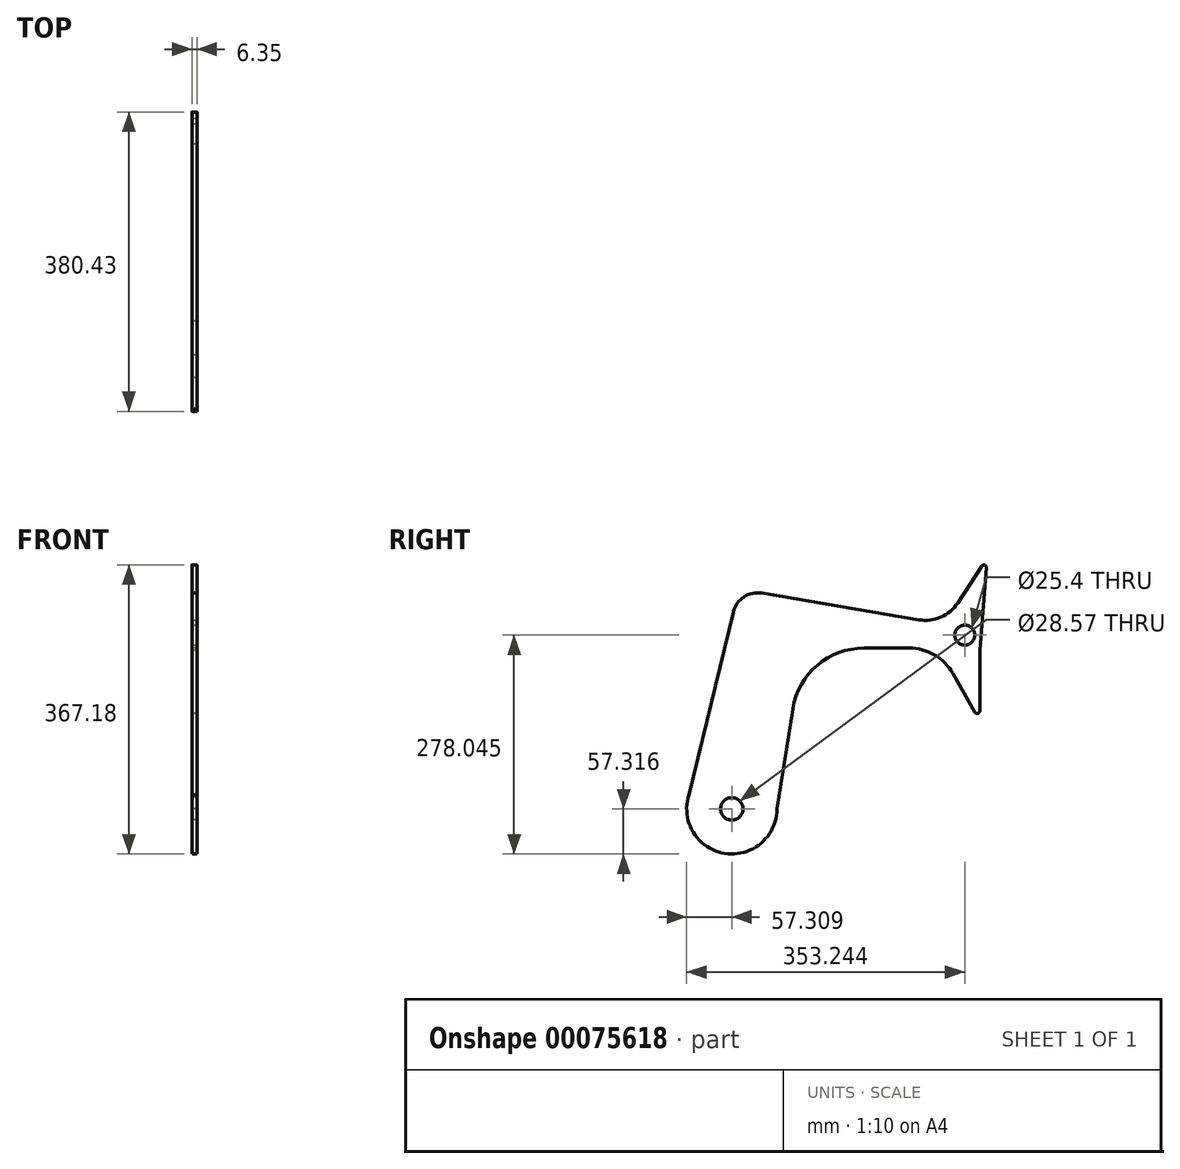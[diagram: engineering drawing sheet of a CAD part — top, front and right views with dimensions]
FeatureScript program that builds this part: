
annotation { "Feature Type Name" : "Feature", "Feature Type Description" : "" }
export const myFeature = defineFeature(function(context is Context, id is Id, definition is map)
    precondition{}
    {
        {
            var Q0;
            Q0=qCreatedBy(makeId("Right.planeOp"),FACE);
            var sketch = newSketch(context, id + "F0", { "sketchPlane" : qUnion([Q0])});
            skLineSegment(sketch, "E0", {"start": v(-2.1, -204.51) * mm, "end": v(18.16, -77.15) * mm});
            skLineSegment(sketch, "E1", {"start": v(108.55, 0) * mm, "end": v(165.98, 0) * mm});
            skLineSegment(sketch, "E2", {"start": v(255.1, -7.42) * mm, "end": v(263.7, 102.5) * mm});
            skLineSegment(sketch, "E3", {"start": v(258.45, 104.29) * mm, "end": v(227.65, 57.43) * mm});
            skLineSegment(sketch, "E4", {"start": v(178.24, 35.93) * mm, "end": v(-21.04, 69.81) * mm});
            skLineSegment(sketch, "E5", {"start": v(-57.64, 45.7) * mm, "end": v(-113.9, -186.5) * mm});
            skPoint(sketch, "E6.visualSharp", {"position": v(255.68, 0) * mm});
            skPoint(sketch, "E7.visualSharp", {"position": v(30.43, 0) * mm});
            skArc(sketch, "E7.filletArc", {"start": v(108.55, 0) * mm, "mid": v(49.13, -21.9) * mm, "end": v(18.16, -77.15) * mm});
            skPoint(sketch, "E8.visualSharp", {"position": v(-50.58, 74.84) * mm});
            skArc(sketch, "E8.filletArc", {"start": v(-21.04, 69.81) * mm, "mid": v(-44.09, 64.97) * mm, "end": v(-57.64, 45.7) * mm});
            skPoint(sketch, "E9.visualSharp", {"position": v(209.97, 30.54) * mm});
            skArc(sketch, "E9.filletArc", {"start": v(178.24, 35.93) * mm, "mid": v(206.15, 39.33) * mm, "end": v(227.65, 57.43) * mm});
            skLineSegment(sketch, "E10", {"start": v(255.46, 0) * mm, "end": v(255.46, -80.02) * mm});
            skLineSegment(sketch, "E11", {"start": v(249.32, -81.64) * mm, "end": v(221.44, -32.34) * mm});
            skPoint(sketch, "E12", {"position": v(182, 0) * mm});
            skPoint(sketch, "E13.visualSharp", {"position": v(-24.24, -343.7) * mm});
            skPoint(sketch, "E14.visualSharp", {"position": v(-149.22, -332.31) * mm});
            skPoint(sketch, "E15.newPointA", {"position": v(203.14, 0) * mm});
            skPoint(sketch, "E15.newPointB", {"position": v(255.46, 0) * mm});
            skArc(sketch, "E15.filletArc", {"start": v(221.44, -32.34) * mm, "mid": v(198.08, -8.68) * mm, "end": v(165.98, 0) * mm});
            skPoint(sketch, "E16.visualSharp", {"position": v(264.57, 113.6) * mm});
            skArc(sketch, "E16.filletArc", {"start": v(263.7, 102.5) * mm, "mid": v(261.77, 105.42) * mm, "end": v(258.45, 104.29) * mm});
            skPoint(sketch, "E17.visualSharp", {"position": v(255.46, -92.48) * mm});
            skArc(sketch, "E17.filletArc", {"start": v(255.41, -92.4) * mm, "mid": v(255.44, -92.4) * mm, "end": v(255.46, -92.39) * mm});
            skArc(sketch, "E18.filletArc", {"start": v(249.32, -81.64) * mm, "mid": v(253.01, -83.2) * mm, "end": v(255.46, -80.02) * mm});
            skCircle(sketch, "E19", {"center": v(-59.41, -204.28) * mm, "radius": 57.31 * mm});
            skCircle(sketch, "E20", {"center": v(-59.41, -204.28) * mm, "radius": 14.29 * mm});
            skSolve(sketch);
        }
        {
            var Q0;
            Q0=makeQuery(id+"F0.imprint","IMPRINT",FACE,{"disambiguationData":[TD([[makeQuery(id+"F0.imprint","IMPRINT",EDGE,{"derivedFrom":sQuery(id+"F0.wireOp",EDGE,"E0")}),1.0]])]});
            extrude(context, id + "F1", {"entities" : qUnion([Q0]), "depth" : 6.35 * mm});
        }
        {
            var Q0;
            {var subQ0=sQuery(id+"F0.wireOp",EDGE,"E10");Q0=makeQuery(id+"F0.imprint","IMPRINT",FACE,{"disambiguationData":[TD([[makeQuery(id+"F0.imprint","IMPRINT",EDGE,{"derivedFrom":subQ0}),-1.0]])]});}
            extrude(context, id + "F2", {"entities" : qUnion([Q0]), "operationType" : NewBodyOperationType.ADD, "depth" : 6.35 * mm});
        }
        {
            var Q0;
            Q0=makeQuery(id+"F1.opExtrude","CAP_FACE",FACE,{"disambiguationData":[OSD([sQuery(id+"F0.wireOp",EDGE,"E0"),sQuery(id+"F0.wireOp",EDGE,"E1"),sQuery(id+"F0.wireOp",EDGE,"E2"),sQuery(id+"F0.wireOp",EDGE,"E3"),sQuery(id+"F0.wireOp",EDGE,"E4"),sQuery(id+"F0.wireOp",EDGE,"E5"),sQuery(id+"F0.wireOp",EDGE,"E7.filletArc"),sQuery(id+"F0.wireOp",EDGE,"E8.filletArc"),sQuery(id+"F0.wireOp",EDGE,"E9.filletArc"),sQuery(id+"F0.wireOp",EDGE,"e1bb0cd2-49ca-4208-82d9-40ad98cda44d"),sQuery(id+"F0.wireOp",EDGE,"E10"),sQuery(id+"F0.wireOp",EDGE,"E11"),sQuery(id+"F0.wireOp",EDGE,"UkPQ0f5z-xmOE-aKsi-LPIj-pIVzT7c7XED3"),sQuery(id+"F0.wireOp",EDGE,"E13.filletArc"),sQuery(id+"F0.wireOp",EDGE,"E14.filletArc"),sQuery(id+"F0.wireOp",EDGE,"E15.filletArc")])],"isStart":false});
            var sketch = newSketch(context, id + "F3", { "sketchPlane" : qUnion([Q0])});
            skCircle(sketch, "E21", {"center": v(236.52, 16.45) * mm, "radius": 6.35 * mm});
            skSolve(sketch);
        }
        {
            var Q0;
            Q0=sQuery(id+"F3.wireOp",VERTEX,"E21.center");
            var Q1;
            Q1=makeQuery(id+"F1.opExtrude","SWEPT_BODY",BODY,{"disambiguationData":[OSD([sQuery(id+"F0.wireOp",EDGE,"E0"),sQuery(id+"F0.wireOp",EDGE,"E1"),sQuery(id+"F0.wireOp",EDGE,"E2"),sQuery(id+"F0.wireOp",EDGE,"E3"),sQuery(id+"F0.wireOp",EDGE,"E4"),sQuery(id+"F0.wireOp",EDGE,"E5"),sQuery(id+"F0.wireOp",EDGE,"E7.filletArc"),sQuery(id+"F0.wireOp",EDGE,"E8.filletArc"),sQuery(id+"F0.wireOp",EDGE,"E9.filletArc"),sQuery(id+"F0.wireOp",EDGE,"e1bb0cd2-49ca-4208-82d9-40ad98cda44d"),sQuery(id+"F0.wireOp",EDGE,"E10"),sQuery(id+"F0.wireOp",EDGE,"E11"),sQuery(id+"F0.wireOp",EDGE,"UkPQ0f5z-xmOE-aKsi-LPIj-pIVzT7c7XED3"),sQuery(id+"F0.wireOp",EDGE,"E13.filletArc"),sQuery(id+"F0.wireOp",EDGE,"E14.filletArc"),sQuery(id+"F0.wireOp",EDGE,"E15.filletArc")])]});
            hole(context, id + "F4", {"style" : HoleStyle.SIMPLE, "endStyle" : HoleEndStyle.THROUGH, "holeDiameter" : 25.4 * mm, "locations" : qUnion([Q0]), "scope" : qUnion([Q1]), "isTappedThrough" : true});
        }
        {
            var Q0;
            Q0=makeQuery(id+"F0.imprint","IMPRINT",FACE,{"disambiguationData":[TD([[makeQuery(id+"F0.imprint","IMPRINT",EDGE,{"derivedFrom":sQuery(id+"F0.wireOp",EDGE,"E20")}),-1.0]])]});
            extrude(context, id + "F5", {"entities" : qUnion([Q0]), "operationType" : NewBodyOperationType.ADD, "depth" : 6.35 * mm});
        }
    });
